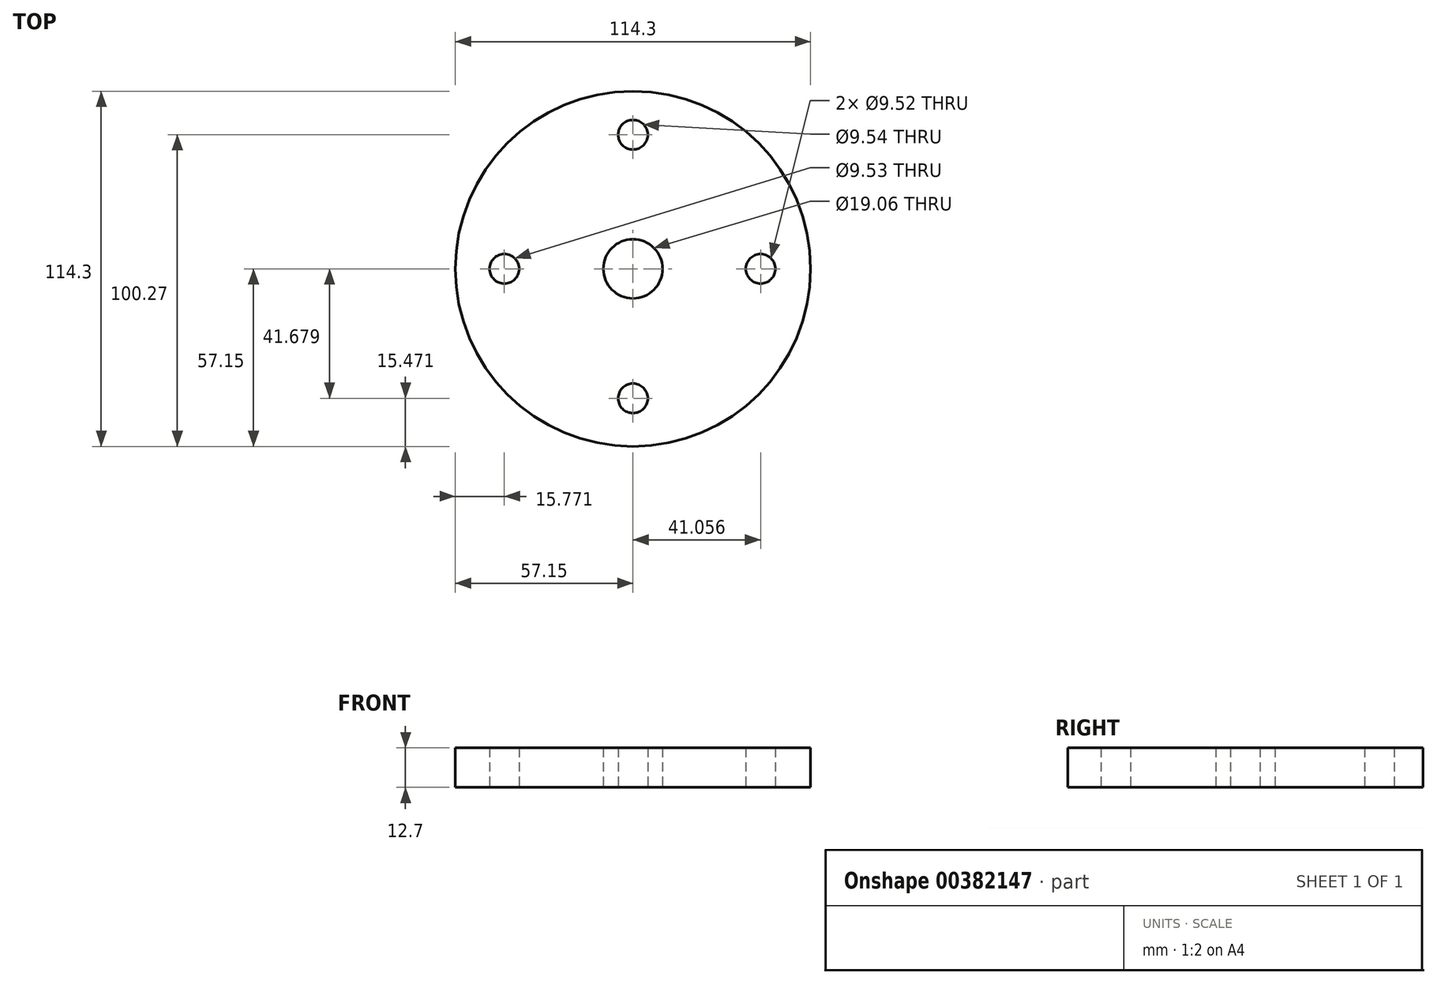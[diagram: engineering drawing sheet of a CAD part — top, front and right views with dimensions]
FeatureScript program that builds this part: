
annotation { "Feature Type Name" : "Feature", "Feature Type Description" : "" }
export const myFeature = defineFeature(function(context is Context, id is Id, definition is map)
    precondition{}
    {
        {
            var Q0;
            Q0=qCreatedBy(makeId("Top.planeOp"),FACE);
            var sketch = newSketch(context, id + "F0", { "sketchPlane" : qUnion([Q0])});
            skCircle(sketch, "E0", {"center": v(0, 0) * mm, "radius": 9.53 * mm});
            skCircle(sketch, "E1", {"center": v(0, 0) * mm, "radius": 57.15 * mm});
            skCircle(sketch, "E2", {"center": v(0, 43.12) * mm, "radius": 4.77 * mm});
            skCircle(sketch, "E3", {"center": v(0, -41.68) * mm, "radius": 4.76 * mm});
            skCircle(sketch, "E4", {"center": v(41.06, 0) * mm, "radius": 4.76 * mm});
            skCircle(sketch, "E5", {"center": v(-41.38, 0) * mm, "radius": 4.77 * mm});
            skSolve(sketch);
        }
        {
            var Q0;
            Q0 = qSketchRegion(id + "F0", true);
            extrude(context, id + "F1", {"entities" : qUnion([Q0]), "depth" : 12.7 * mm});
        }
    });
